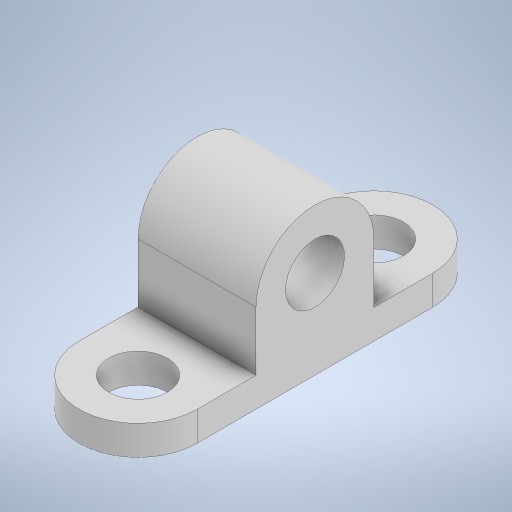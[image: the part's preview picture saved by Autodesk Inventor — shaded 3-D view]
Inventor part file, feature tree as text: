
AUTODESK INVENTOR PART (.ipt)
format: ipt  version: 2024.2 (Build 282272000, 272)  size: 289,792 bytes
history: native  units: in
note: dims shown in document units (in); Inventor stores cm internally (conversion verified against a paired STEP export)
features: extrude x7, sketch x7
ambient origin geometry x8: Origin, YZ Plane, XZ Plane, XY Plane, X Axis, Y Axis, Z Axis, Center Point
bodies: Solid1 (feature_tree)
feature tree (14):
  extrude  "Extrusion1"  TaperAngle=90.0deg  [1 undecoded]
  extrude  "Extrusion2"  Depth=0.3937in
  extrude  "Extrusion3"  Depth=0.7874in
  extrude  "Extrusion4"  Depth=0.7874in
  extrude  "Extrusion5"  Depth=1.5748in TaperAngle=0.0deg
  extrude  "Extrusion6"  Depth=0.7874in TaperAngle=0.0deg
  extrude  "Extrusion7"  Depth=0.7874in TaperAngle=0.0deg
  sketch  "Sketch1"  dims[d0=0.7874in d1=90.0deg]
  sketch  "Sketch2"  dims[d2=0.7874in d3=0.3937in]
  sketch  "Sketch3"  dims[d4=0.7874in d5=0.7874in]
  sketch  "Sketch4"  dims[d7=0.7874in d8=0.7874in]
  sketch  "Sketch5"  dims[d9=0.7874in d10=1.5748in d11=0.0in]
  sketch  "Sketch6"  dims[d12=0.3937in d13=0.7874in d14=0.0in]
  sketch  "Sketch7"  dims[d15=0.3937in d16=0.7874in d17=0.0in d18=1.5748in d19=0.7874in d20=0.3937in d21=0.0in d22=0.7874in d23=0.3937in d24=0.0in d25=1.5748in d26=0.7874in d27=0.3937in d28=0.0in d29=0.7874in d30=0.3937in d31=0.0in]
note: 1 required parameter value undecoded (feature->parameter linkage not recoverable at this tier; creation-order binding heuristic only, values carry confidence <= 0.55)
